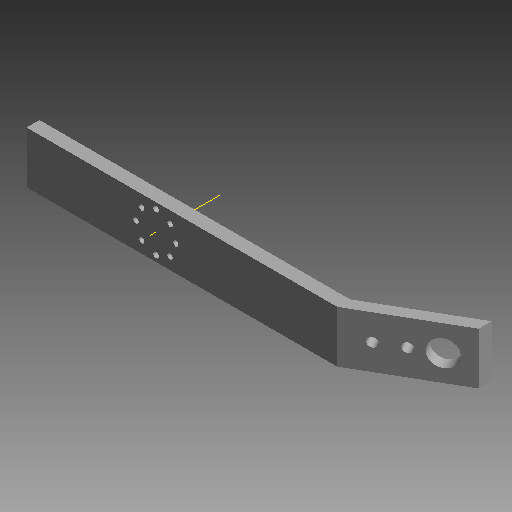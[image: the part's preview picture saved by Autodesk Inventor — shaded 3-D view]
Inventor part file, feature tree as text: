
AUTODESK INVENTOR PART (.ipt)
format: ipt  version: 2019 (Build 230136000, 136)  size: 96,256 bytes
history: native  units: mm (DEFAULTED — no unit token found)
features: other x4, sketch x4
ambient origin geometry x8: Origin, YZ Plane, XZ Plane, XY Plane, X Axis, Y Axis, Z Axis, Center Point
bodies: Solid1 (feature_tree)
feature tree (8):
  other  "Wheel Arms.ipt"
  other  "Solid1::Wheel Arms.ipt"
  other  "TaggingFeature1"
  sketch  "Sketch1"  dims[d0=10.0mm]
  sketch  "Sketch4"
  sketch  "Sketch9"
  sketch  "Sketch10"
  other  "Work Axis1"
